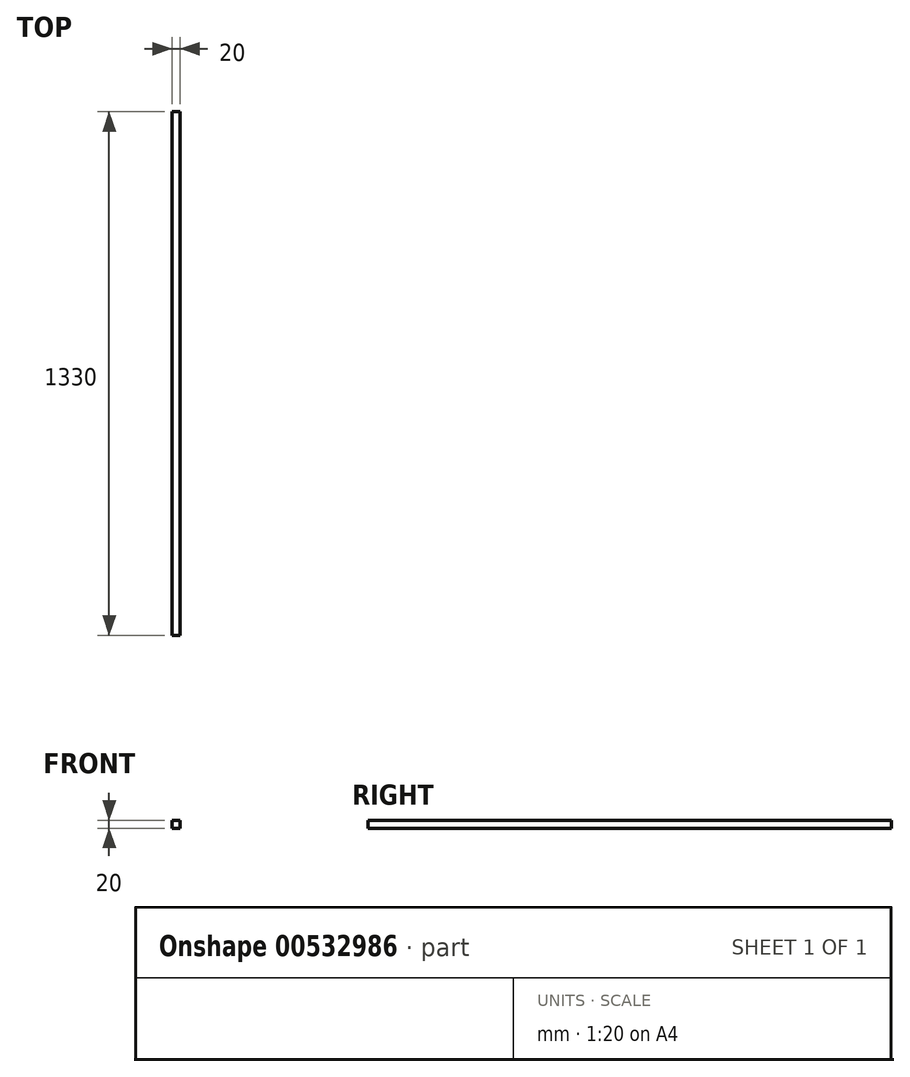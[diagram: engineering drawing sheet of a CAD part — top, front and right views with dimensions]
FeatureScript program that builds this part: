
annotation { "Feature Type Name" : "Feature", "Feature Type Description" : "" }
export const myFeature = defineFeature(function(context is Context, id is Id, definition is map)
    precondition{}
    {
        {
            var Q0;
            Q0=qCreatedBy(makeId("Front.planeOp"),FACE);
            var sketch = newSketch(context, id + "F0", { "sketchPlane" : qUnion([Q0])});
            skLineSegment(sketch, "E0.bottom", {"start": v(6.1, 22.76) * mm, "end": v(26.1, 22.76) * mm});
            skLineSegment(sketch, "E0.top", {"start": v(6.1, 2.76) * mm, "end": v(26.1, 2.76) * mm});
            skLineSegment(sketch, "E0.left", {"start": v(6.1, 22.76) * mm, "end": v(6.1, 2.76) * mm});
            skLineSegment(sketch, "E0.right", {"start": v(26.1, 22.76) * mm, "end": v(26.1, 2.76) * mm});
            skSolve(sketch);
        }
        {
            var Q0;
            Q0 = qSketchRegion(id + "F0", true);
            extrude(context, id + "F1", {"entities" : qUnion([Q0]), "oppositeDirection" : true, "depth" : 1330 * mm, "offsetDistance" : 25 * mm});
        }
    });
